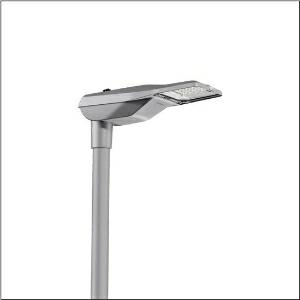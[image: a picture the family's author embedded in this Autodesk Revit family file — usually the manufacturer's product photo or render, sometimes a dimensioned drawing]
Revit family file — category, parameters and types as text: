
# Revit family: streetlight_sl_21_micro___st1_5a_5xe1p43s08db_ce40
name_source: partatom
category: Lighting Fixtures
units: mm (PartAtom-declared; Revit-internal decimal feet)

## family parameters
Cut with Voids When Loaded = No
Host = Face
Light Source = No
Part Type = Normal
Room Calculation Point = No
Round Connector Dimension = Use Diameter
Shared = No

## types (1)
- --- (1 x LED, 5230 lm, 39.1 W, 4000K)
    Apparent Load = 39 VA
    CIE Flux Codes = 22 53 95 100 100
    Color Rendering = 70
    Color Temperature = 4000K
    Default Elevation = 1800 mm
    Description = Streetlight SL 21 micro, mast luminaire, primary light control with lens, of PMMA, primary optical cover: cover, of toughened safety glass, transparent, light distribution: ST1.5a, light emission: direct distribution, primary light characteristic: asymmetric, installation type: side-entry, post-top, LED, High Power LED, rated luminous flux: 5.230lm, luminous efficacy: 134lm/W, light colour: 740, colour temperature: 4000K, control gear: D4i, control: flexible luminous flux parameterisation, time-dependent luminous flux control, constant luminous flux control, overheat protection, pre-setting: logarithmic dimming characteristic, mains connection: 220..240V, AC, 50/60Hz, start of lifetime: 39W, end of service life: 41W, reduction: 18W, luminaire housing, of diecast aluminium, powder-coated, Siteco® metallic grey (DB 702S), corrosivity category C5 mid according to DIN EN ISO 12944, please order mast flange separately, inclination adjustable: 0°, 5°, 10°, 15°, sealing non-destructively replaceable, multi-level sealing system, length: 528mm, width: 235mm, height: 110mm, mast flange for spigot size: 42mm (side-entry): 5XC10008XM4, 60/48mm (side-entry/post-top): 5XC10108XM2, 76/60mm (side-entry/post-top): 5XC10108XM1, Smart Interface above, protection rating (complete): IP66, insulation class (complete): insulation class II (safety insulation), certification: CE, ENEC, ENEC+, VDE, impact resistance: IK10, permissible operating ambient temperature for outdoor applications: -40..+50°C, standard-compliant lighting for roads and squares, packaging unit: 1 piece

Light Distribution: ST1.5a
    Height = 110 mm
    Lamp = 1 x LED
    Lamp Light Flux = 5230 lm
    Lamp Power = 39.1 W
    Lamp count = 1
    Length = 528 mm
    Luminous efficacy = 134 lm/W
    Manufacturer = Siteco
    ModVariant = No
    Model = 5XE1P43S08DB
    Number of Poles = 1
    OnlyDefault = Yes
    Power Factor = 1
    Product Name = Streetlight SL 21 micro | ST1.5a
    Product group = mast luminaire | pylon top
    ProductGroupID = 6100
    Protection Class = Protection class II
    Protection Degree = IP 66
    RLX_Detail_Level = 1
    RLX_Emergency_Light_Flux = 0 lm
    RLX_Emergency_Type = 0
    RLX_Emergency_Type_DB = No
    RlxData = <blob elided: 102469 chars, md5=69600793>
    Socket = socket
    Standby Power = 0 W
    System Light Flux = 5230 lm
    System Power = 39 W
    Type Comments = factory setting: luminous flux: 100 % | dim-lin: 254 | 765 mA
    Type Image = l_1277292.jpg
    URL = http://relux.com
    VarID = @adj_175191
    Voltage = 0 V
    Weight = 0.00 kg
    Width = 235 mm

## geometry (parser evidence)
native form markers: Blend x4, Sweep x11
no freeform markers — native parametric forms only
